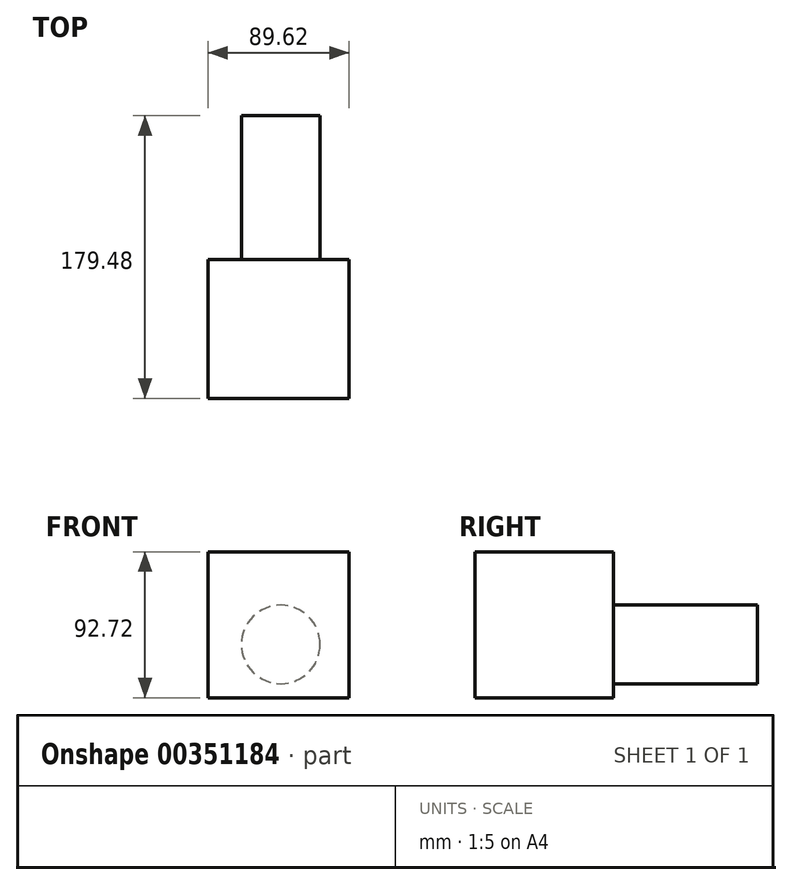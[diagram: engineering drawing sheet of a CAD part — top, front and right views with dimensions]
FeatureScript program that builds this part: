
annotation { "Feature Type Name" : "Feature", "Feature Type Description" : "" }
export const myFeature = defineFeature(function(context is Context, id is Id, definition is map)
    precondition{}
    {
        {
            var Q0;
            Q0=qCreatedBy(makeId("Front.planeOp"),FACE);
            var sketch = newSketch(context, id + "F0", { "sketchPlane" : qUnion([Q0])});
            skLineSegment(sketch, "E0.bottom", {"start": v(43.33, 58.86) * mm, "end": v(-46.3, 58.86) * mm});
            skLineSegment(sketch, "E0.top", {"start": v(43.33, -33.86) * mm, "end": v(-46.3, -33.86) * mm});
            skLineSegment(sketch, "E0.left", {"start": v(43.33, 58.86) * mm, "end": v(43.33, -33.86) * mm});
            skLineSegment(sketch, "E0.right", {"start": v(-46.3, 58.86) * mm, "end": v(-46.3, -33.86) * mm});
            skSolve(sketch);
        }
        {
            var Q0;
            Q0=makeQuery(id+"F0.imprint","IMPRINT",FACE,{"disambiguationData":[TD([[makeQuery(id+"F0.imprint","IMPRINT",EDGE,{"derivedFrom":sQuery(id+"F0.wireOp",EDGE,"E0.bottom")}),1.0]])]});
            extrude(context, id + "F1", {"entities" : qUnion([Q0]), "depth" : 88.08 * mm});
        }
        {
            var Q0;
            Q0=makeQuery(id+"F1.opExtrude","CAP_FACE",FACE,{"disambiguationData":[OSD([sQuery(id+"F0.wireOp",EDGE,"E0.bottom"),sQuery(id+"F0.wireOp",EDGE,"E0.top"),sQuery(id+"F0.wireOp",EDGE,"E0.left"),sQuery(id+"F0.wireOp",EDGE,"E0.right")])],"isStart":false});
            var sketch = newSketch(context, id + "F2", { "sketchPlane" : qUnion([Q0])});
            skCircle(sketch, "E1", {"center": v(0, 0) * mm, "radius": 24.95 * mm});
            skSolve(sketch);
        }
        {
            var Q0;
            Q0=makeQuery(id+"F2.imprint","IMPRINT",FACE,{"disambiguationData":[TD([[makeQuery(id+"F2.imprint","IMPRINT",EDGE,{"derivedFrom":sQuery(id+"F2.wireOp",EDGE,"E1")}),1.0]])]});
            extrude(context, id + "F3", {"entities" : qUnion([Q0]), "operationType" : NewBodyOperationType.ADD, "oppositeDirection" : true, "depth" : 179.48 * mm});
        }
    });
